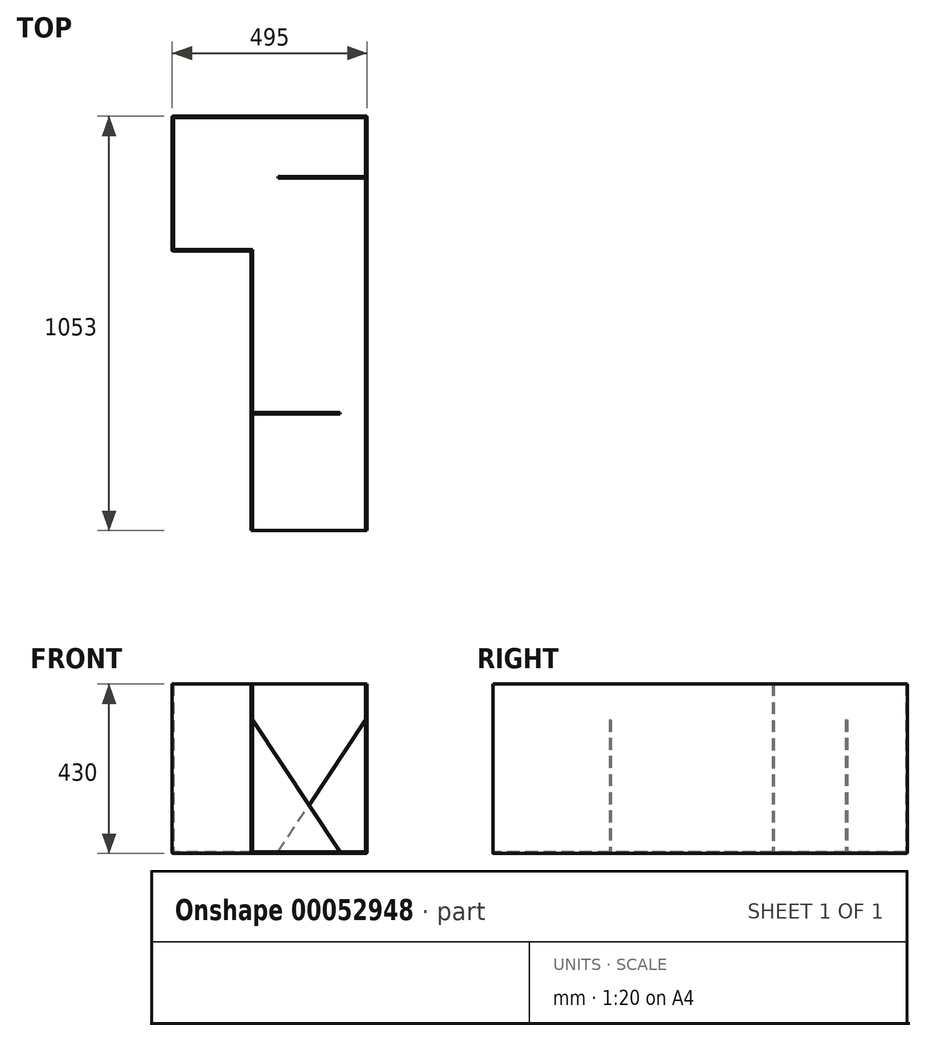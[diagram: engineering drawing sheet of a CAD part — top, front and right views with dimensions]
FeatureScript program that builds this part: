
annotation { "Feature Type Name" : "Feature", "Feature Type Description" : "" }
export const myFeature = defineFeature(function(context is Context, id is Id, definition is map)
    precondition{}
    {
        {
            var Q0;
            Q0=qCreatedBy(makeId("Top.planeOp"),FACE);
            var sketch = newSketch(context, id + "F0", { "sketchPlane" : qUnion([Q0])});
            skLineSegment(sketch, "E0", {"start": v(0, 0) * mm, "end": v(495, 0) * mm});
            skLineSegment(sketch, "E1", {"start": v(200, -343) * mm, "end": v(0, -343) * mm});
            skLineSegment(sketch, "E2", {"start": v(0, -343) * mm, "end": v(0, 0) * mm});
            skLineSegment(sketch, "E3.right", {"start": v(200, -343) * mm, "end": v(200, -1053) * mm});
            skLineSegment(sketch, "E4.left", {"start": v(495, 0) * mm, "end": v(495, -1053) * mm});
            skLineSegment(sketch, "E5.0", {"start": v(491, -4) * mm, "end": v(491, -1053) * mm});
            skLineSegment(sketch, "E5.1", {"start": v(204, -339) * mm, "end": v(204, -1053) * mm});
            skLineSegment(sketch, "E5.2", {"start": v(204, -339) * mm, "end": v(4, -339) * mm});
            skLineSegment(sketch, "E5.3", {"start": v(4, -339) * mm, "end": v(4, -4) * mm});
            skLineSegment(sketch, "E5.4", {"start": v(4, -4) * mm, "end": v(491, -4) * mm});
            skLineSegment(sketch, "E6", {"start": v(204, -1053) * mm, "end": v(200, -1053) * mm});
            skLineSegment(sketch, "E7", {"start": v(491, -1053) * mm, "end": v(495, -1053) * mm});
            skSolve(sketch);
        }
        {
            var Q0;
            Q0=makeQuery(id+"F0.imprint","IMPRINT",FACE,{"disambiguationData":[TD([[makeQuery(id+"F0.imprint","IMPRINT",EDGE,{"derivedFrom":sQuery(id+"F0.wireOp",EDGE,"E0")}),-1.0]])]});
            extrude(context, id + "F1", {"entities" : qUnion([Q0]), "depth" : 426 * mm});
        }
        {
            var Q0;
            Q0=qCreatedBy(makeId("Top.planeOp"),FACE);
            var sketch = newSketch(context, id + "F2", { "sketchPlane" : qUnion([Q0])});
            skLineSegment(sketch, "E8.0", {"start": v(200, -343) * mm, "end": v(0, -343) * mm});
            skLineSegment(sketch, "E9.0", {"start": v(0, -343) * mm, "end": v(0, 0) * mm});
            skLineSegment(sketch, "E10.0", {"start": v(0, 0) * mm, "end": v(0, 0) * mm});
            skLineSegment(sketch, "E11.0", {"start": v(0, 0) * mm, "end": v(495, 0) * mm});
            skLineSegment(sketch, "E12.0", {"start": v(200, -343) * mm, "end": v(200, -343) * mm});
            skLineSegment(sketch, "E13.0", {"start": v(495, 0) * mm, "end": v(495, 0) * mm});
            skLineSegment(sketch, "E14.0", {"start": v(495, 0) * mm, "end": v(495, -1053) * mm});
            skLineSegment(sketch, "E15", {"start": v(495, -1053) * mm, "end": v(199.99, -1053) * mm});
            skLineSegment(sketch, "E16", {"start": v(199.99, -1053) * mm, "end": v(200, -343) * mm});
            skSolve(sketch);
        }
        {
            var Q0;
            Q0=qSketchRegion(id+"F2",true);
            extrude(context, id + "F3", {"entities" : qUnion([Q0]), "operationType" : NewBodyOperationType.ADD, "oppositeDirection" : true, "depth" : 4 * mm});
        }
        {
            var Q0;
            Q0=makeQuery(id+"F3.opExtrude","CAP_EDGE",EDGE,{"disambiguationData":[OSD([sQuery(id+"F2.wireOp",EDGE,"E13.0")])],"isStart":false});
            var Q1;
            Q1=makeQuery(id+"F3.opExtrude","CAP_EDGE",EDGE,{"disambiguationData":[OSD([sQuery(id+"F2.wireOp",EDGE,"E8.0")])],"isStart":false});
            var Q2;
            Q2=makeQuery(id+"F3.opExtrude","CAP_EDGE",EDGE,{"disambiguationData":[OSD([sQuery(id+"F2.wireOp",EDGE,"E12.0")])],"isStart":false});
            var Q3;
            Q3=makeQuery(id+"F3.opExtrude","CAP_EDGE",EDGE,{"disambiguationData":[OSD([sQuery(id+"F2.wireOp",EDGE,"E9.0")])],"isStart":false});
            var Q4;
            Q4=makeQuery(id+"F3.opExtrude","CAP_EDGE",EDGE,{"disambiguationData":[OSD([sQuery(id+"F2.wireOp",EDGE,"E11.0")])],"isStart":false});
            var Q5;
            Q5=makeQuery(id+"F3.boolean.opBoolean","MERGE",EDGE,{"derivedFrom":[makeQuery(id+"F1.opExtrude","SWEPT_EDGE",EDGE,{"disambiguationData":[OSD([sQuery(id+"F0.wireOp",EDGE,"E1"),sQuery(id+"F0.wireOp",EDGE,"E3.right")])]}),makeQuery(id+"F3.opExtrude","SWEPT_EDGE",EDGE,{"disambiguationData":[OSD([sQuery(id+"F2.wireOp",EDGE,"E8.0"),sQuery(id+"F2.wireOp",EDGE,"E12.0")])]})]});
            var Q6;
            Q6=makeQuery(id+"F3.boolean.opBoolean","MERGE",EDGE,{"derivedFrom":[makeQuery(id+"F1.opExtrude","SWEPT_EDGE",EDGE,{"disambiguationData":[OSD([sQuery(id+"F0.wireOp",EDGE,"E1"),sQuery(id+"F0.wireOp",EDGE,"E2")])]}),makeQuery(id+"F3.opExtrude","SWEPT_EDGE",EDGE,{"disambiguationData":[OSD([sQuery(id+"F2.wireOp",EDGE,"E8.0"),sQuery(id+"F2.wireOp",EDGE,"E9.0")])]})]});
            var Q7;
            Q7=makeQuery(id+"F3.boolean.opBoolean","MERGE",EDGE,{"derivedFrom":[makeQuery(id+"F1.opExtrude","SWEPT_EDGE",EDGE,{"disambiguationData":[OSD([sQuery(id+"F0.wireOp",EDGE,"E0"),sQuery(id+"F0.wireOp",EDGE,"E2")])]}),makeQuery(id+"F3.opExtrude","SWEPT_EDGE",EDGE,{"disambiguationData":[OSD([sQuery(id+"F2.wireOp",EDGE,"E9.0"),sQuery(id+"F2.wireOp",EDGE,"E11.0")])]})]});
            var Q8;
            Q8=makeQuery(id+"F1.opExtrude","SWEPT_EDGE",EDGE,{"disambiguationData":[OSD([sQuery(id+"F0.wireOp",EDGE,"41269a5a-69f6-4670-b1a7-19bf830e781a"),sQuery(id+"F0.wireOp",EDGE,"E4.right")])]});
            var Q9;
            Q9=makeQuery(id+"F1.opExtrude","SWEPT_EDGE",EDGE,{"disambiguationData":[OSD([sQuery(id+"F0.wireOp",EDGE,"cc5772d9-c29a-4c81-bde5-837d5d9decb7"),sQuery(id+"F0.wireOp",EDGE,"E3.left")])]});
            var Q10;
            Q10=makeQuery(id+"F1.opExtrude","SWEPT_EDGE",EDGE,{"disambiguationData":[OSD([sQuery(id+"F0.wireOp",EDGE,"41269a5a-69f6-4670-b1a7-19bf830e781a"),sQuery(id+"F0.wireOp",EDGE,"05cfef9b-c223-4bdb-b400-77ea615546ad")])]});
            var Q11;
            Q11=makeQuery(id+"F1.opExtrude","SWEPT_EDGE",EDGE,{"disambiguationData":[OSD([sQuery(id+"F0.wireOp",EDGE,"05cfef9b-c223-4bdb-b400-77ea615546ad"),sQuery(id+"F0.wireOp",EDGE,"cc5772d9-c29a-4c81-bde5-837d5d9decb7")])]});
            var Q12;
            Q12=makeQuery(id+"F3.boolean.opBoolean","MERGE",EDGE,{"derivedFrom":[makeQuery(id+"F1.opExtrude","SWEPT_EDGE",EDGE,{"disambiguationData":[OSD([sQuery(id+"F0.wireOp",EDGE,"E0"),sQuery(id+"F0.wireOp",EDGE,"E4.left")])]}),makeQuery(id+"F3.opExtrude","SWEPT_EDGE",EDGE,{"disambiguationData":[OSD([sQuery(id+"F2.wireOp",EDGE,"E11.0"),sQuery(id+"F2.wireOp",EDGE,"E13.0")])]})]});
            var Q13;
            Q13=makeQuery(id+"F3.opExtrude","CAP_EDGE",EDGE,{"disambiguationData":[OSD([sQuery(id+"F2.wireOp",EDGE,"E16")])],"isStart":false});
            var Q14;
            Q14=makeQuery(id+"F3.opExtrude","CAP_EDGE",EDGE,{"disambiguationData":[OSD([sQuery(id+"F2.wireOp",EDGE,"E14.0")])],"isStart":false});
            fillet(context, id + "F4", {"entities" : qUnion([Q0, Q1, Q2, Q3, Q4, Q5, Q6, Q7, Q8, Q9, Q10, Q11, Q12, Q13, Q14]), "radius" : 2 * mm, "tangentPropagation" : true, "allowEdgeOverflow" : false});
        }
        {
            var Q0;
            Q0=makeQuery(id+"F3.boolean.opBoolean","MERGE",FACE,{"derivedFrom":[makeQuery(id+"F1.opExtrude","SWEPT_FACE",FACE,{"disambiguationData":[OSD([sQuery(id+"F0.wireOp",EDGE,"E6")])]}),makeQuery(id+"F1.opExtrude","SWEPT_FACE",FACE,{"disambiguationData":[OSD([sQuery(id+"F0.wireOp",EDGE,"E7")])]}),makeQuery(id+"F3.opExtrude","SWEPT_FACE",FACE,{"disambiguationData":[OSD([sQuery(id+"F2.wireOp",EDGE,"E15")])]})]});
            cPlane(context, id + "F5", {"entities" : qUnion([Q0]), "cplaneType" : CPlaneType.OFFSET, "offset" : 300 * mm, "oppositeDirection" : true, "width" : 150 * mm, "height" : 150 * mm});
        }
        {
            var Q0;
            Q0=qCreatedBy(id+"F5.planeOp",FACE);
            var sketch = newSketch(context, id + "F6", { "sketchPlane" : qUnion([Q0])});
            skLineSegment(sketch, "E17", {"start": v(204, 335) * mm, "end": v(426, 0) * mm});
            skLineSegment(sketch, "E18", {"start": v(204, 335) * mm, "end": v(204, 0) * mm});
            skLineSegment(sketch, "E19", {"start": v(204, 0) * mm, "end": v(426, 0) * mm});
            skSolve(sketch);
        }
        {
            var Q0;
            Q0 = qSketchRegion(id + "F6", true);
            extrude(context, id + "F7", {"entities" : qUnion([Q0]), "operationType" : NewBodyOperationType.ADD, "depth" : 4 * mm});
        }
        {
            var Q0;
            Q0 = qSketchRegion(id + "F6", true);
            extrude(context, id + "F8", {"entities" : qUnion([Q0]), "operationType" : NewBodyOperationType.ADD, "depth" : 4 * mm});
        }
        {
            var Q0;
            Q0=qCreatedBy(id+"F5.planeOp",FACE);
            cPlane(context, id + "F9", {"entities" : qUnion([Q0]), "cplaneType" : CPlaneType.OFFSET, "offset" : 600 * mm, "oppositeDirection" : true, "width" : 150 * mm, "height" : 150 * mm});
        }
        {
            var Q0;
            Q0=qCreatedBy(id+"F9.planeOp",FACE);
            var sketch = newSketch(context, id + "F10", { "sketchPlane" : qUnion([Q0])});
            skLineSegment(sketch, "E20", {"start": v(269, 0) * mm, "end": v(491, 335) * mm});
            skLineSegment(sketch, "E21", {"start": v(491, 335) * mm, "end": v(491, 0) * mm});
            skLineSegment(sketch, "E22", {"start": v(491, 0) * mm, "end": v(269, 0) * mm});
            skSolve(sketch);
        }
        {
            var Q0;
            Q0 = qSketchRegion(id + "F10", true);
            extrude(context, id + "F11", {"entities" : qUnion([Q0]), "operationType" : NewBodyOperationType.ADD, "depth" : 4 * mm});
        }
    });
